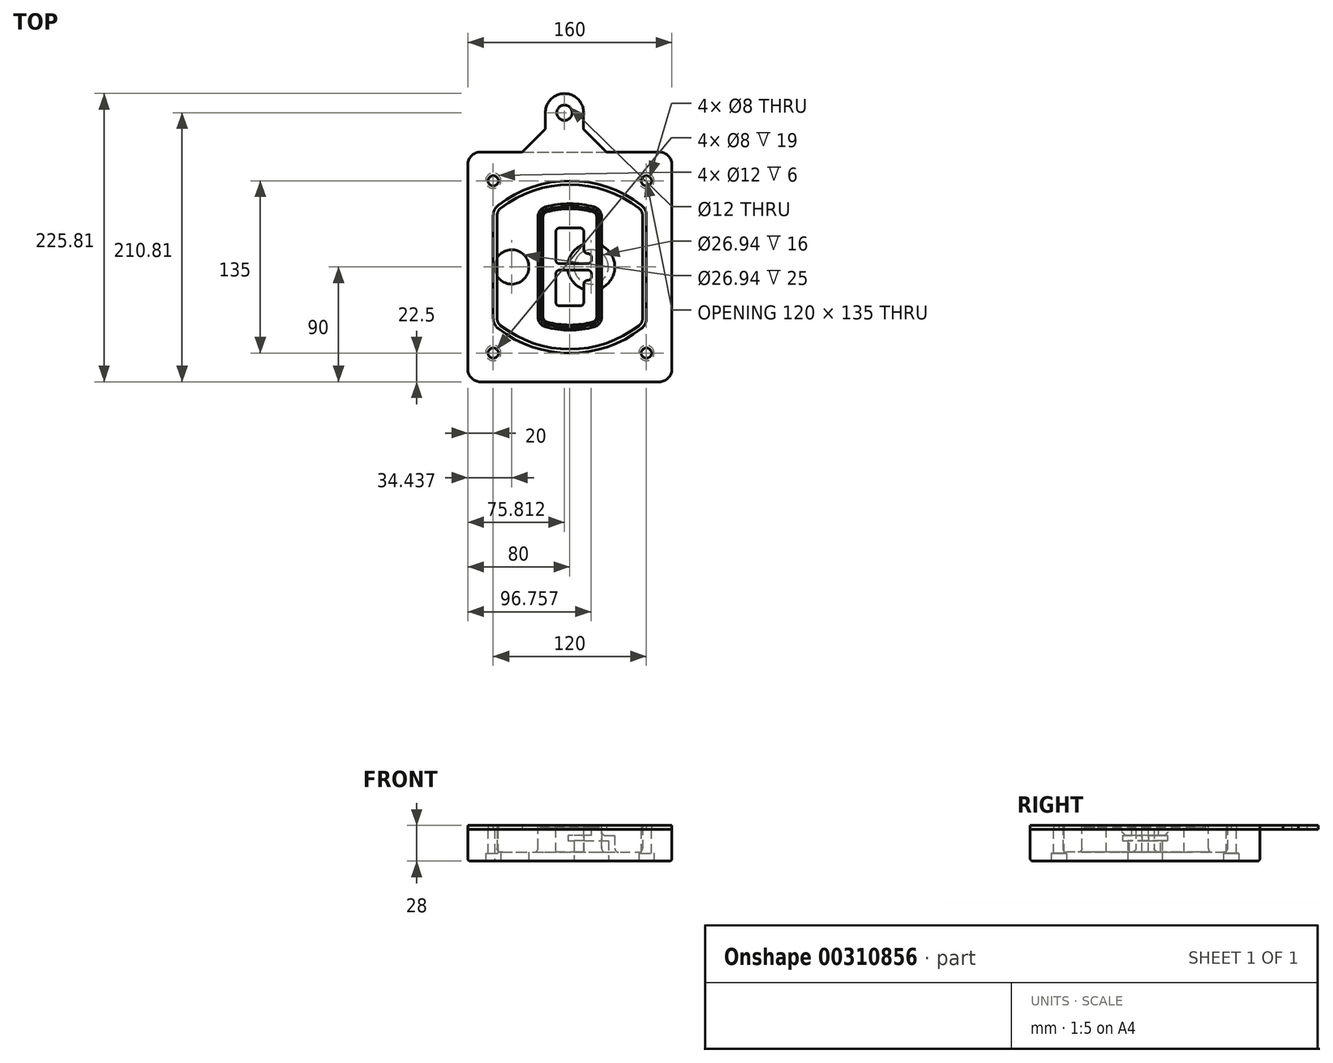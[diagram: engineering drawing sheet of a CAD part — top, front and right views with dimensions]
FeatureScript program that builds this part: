
annotation { "Feature Type Name" : "Feature", "Feature Type Description" : "" }
export const myFeature = defineFeature(function(context is Context, id is Id, definition is map)
    precondition{}
    {
        {
            var Q0;
            Q0=qCreatedBy(makeId("Top.planeOp"),FACE);
            var sketch = newSketch(context, id + "F0", { "sketchPlane" : qUnion([Q0])});
            skPoint(sketch, "E0.rect.middle", {"position": v(0, 0) * mm});
            skLineSegment(sketch, "E1.bottom", {"start": v(-70, -90) * mm, "end": v(70, -90) * mm});
            skLineSegment(sketch, "E1.top", {"start": v(-70, 90) * mm, "end": v(70, 90) * mm});
            skLineSegment(sketch, "E1.left", {"start": v(-80, -80) * mm, "end": v(-80, 80) * mm});
            skLineSegment(sketch, "E1.right", {"start": v(80, -80) * mm, "end": v(80, 80) * mm});
            skLineSegment(sketch, "E2", {"start": v(-80, 90) * mm, "end": v(80, -90) * mm, "construction": true});
            skLineSegment(sketch, "E3", {"start": v(80, 90) * mm, "end": v(-80, -90) * mm, "construction": true});
            skCircle(sketch, "E4", {"center": v(-60, 67.5) * mm, "radius": 4 * mm});
            skCircle(sketch, "E5", {"center": v(60, 67.5) * mm, "radius": 4 * mm});
            skCircle(sketch, "E6", {"center": v(60, -67.5) * mm, "radius": 4 * mm});
            skCircle(sketch, "E7", {"center": v(-60, -67.5) * mm, "radius": 4 * mm});
            skLineSegment(sketch, "E8", {"start": v(-60, 67.5) * mm, "end": v(60, 67.5) * mm, "construction": true});
            skLineSegment(sketch, "E9", {"start": v(60, 67.5) * mm, "end": v(60, -67.5) * mm, "construction": true});
            skLineSegment(sketch, "E10", {"start": v(60, -67.5) * mm, "end": v(-60, -67.5) * mm, "construction": true});
            skLineSegment(sketch, "E11", {"start": v(-60, -67.5) * mm, "end": v(-60, 67.5) * mm, "construction": true});
            skLineSegment(sketch, "E12", {"start": v(-60, 40.3) * mm, "end": v(-60, -40.3) * mm});
            skLineSegment(sketch, "E13", {"start": v(60, 40.3) * mm, "end": v(60, -40.3) * mm});
            skArc(sketch, "E14", {"start": v(56.15, 48.18) * mm, "mid": v(0, 67.5) * mm, "end": v(-56.15, 48.18) * mm});
            skArc(sketch, "E15", {"start": v(-56.15, -48.18) * mm, "mid": v(0, -67.5) * mm, "end": v(56.15, -48.18) * mm});
            skLineSegment(sketch, "E16", {"start": v(-60, 0) * mm, "end": v(60, 0) * mm, "construction": true});
            skPoint(sketch, "E17.visualSharp", {"position": v(-60, -45) * mm});
            skArc(sketch, "E17.filletArc", {"start": v(-60, -40.3) * mm, "mid": v(-58.99, -44.68) * mm, "end": v(-56.15, -48.18) * mm});
            skPoint(sketch, "E18.visualSharp", {"position": v(-60, 45) * mm});
            skArc(sketch, "E18.filletArc", {"start": v(-56.15, 48.18) * mm, "mid": v(-58.99, 44.68) * mm, "end": v(-60, 40.3) * mm});
            skPoint(sketch, "E19.visualSharp", {"position": v(60, 45) * mm});
            skArc(sketch, "E19.filletArc", {"start": v(60, 40.3) * mm, "mid": v(58.99, 44.68) * mm, "end": v(56.15, 48.18) * mm});
            skPoint(sketch, "E20.visualSharp", {"position": v(60, -45) * mm});
            skArc(sketch, "E20.filletArc", {"start": v(56.15, -48.18) * mm, "mid": v(58.99, -44.68) * mm, "end": v(60, -40.3) * mm});
            skPoint(sketch, "E21.visualSharp", {"position": v(-80, 90) * mm});
            skArc(sketch, "E21.filletArc", {"start": v(-70, 90) * mm, "mid": v(-77.07, 87.07) * mm, "end": v(-80, 80) * mm});
            skPoint(sketch, "E22.visualSharp", {"position": v(80, 90) * mm});
            skArc(sketch, "E22.filletArc", {"start": v(80, 80) * mm, "mid": v(77.07, 87.07) * mm, "end": v(70, 90) * mm});
            skPoint(sketch, "E23.visualSharp", {"position": v(80, -90) * mm});
            skArc(sketch, "E23.filletArc", {"start": v(70, -90) * mm, "mid": v(77.07, -87.07) * mm, "end": v(80, -80) * mm});
            skPoint(sketch, "E24.visualSharp", {"position": v(-80, -90) * mm});
            skArc(sketch, "E24.filletArc", {"start": v(-80, -80) * mm, "mid": v(-77.07, -87.07) * mm, "end": v(-70, -90) * mm});
            skArc(sketch, "E25.0", {"start": v(57, 40.3) * mm, "mid": v(56.3, 43.36) * mm, "end": v(54.3, 45.81) * mm});
            skLineSegment(sketch, "E25.1", {"start": v(57, 40.3) * mm, "end": v(57, -40.3) * mm});
            skArc(sketch, "E25.2", {"start": v(54.3, -45.81) * mm, "mid": v(56.3, -43.36) * mm, "end": v(57, -40.3) * mm});
            skArc(sketch, "E25.3", {"start": v(-54.3, -45.81) * mm, "mid": v(0, -64.5) * mm, "end": v(54.3, -45.81) * mm});
            skArc(sketch, "E25.4", {"start": v(-57, -40.3) * mm, "mid": v(-56.3, -43.36) * mm, "end": v(-54.3, -45.81) * mm});
            skArc(sketch, "E25.5", {"start": v(54.3, 45.81) * mm, "mid": v(0, 64.5) * mm, "end": v(-54.3, 45.81) * mm});
            skLineSegment(sketch, "E25.6", {"start": v(-57, 40.3) * mm, "end": v(-57, -40.3) * mm});
            skArc(sketch, "E25.7", {"start": v(-54.3, 45.81) * mm, "mid": v(-56.3, 43.36) * mm, "end": v(-57, 40.3) * mm});
            skArc(sketch, "E26.0", {"start": v(-58.62, 51.33) * mm, "mid": v(-62.58, 46.43) * mm, "end": v(-64, 40.3) * mm});
            skArc(sketch, "E26.1", {"start": v(58.62, 51.33) * mm, "mid": v(0, 71.5) * mm, "end": v(-58.62, 51.33) * mm});
            skArc(sketch, "E26.2", {"start": v(64, 40.3) * mm, "mid": v(62.58, 46.43) * mm, "end": v(58.62, 51.33) * mm});
            skLineSegment(sketch, "E26.3", {"start": v(64, 40.3) * mm, "end": v(64, -40.3) * mm});
            skArc(sketch, "E26.4", {"start": v(58.62, -51.33) * mm, "mid": v(62.58, -46.43) * mm, "end": v(64, -40.3) * mm});
            skLineSegment(sketch, "E26.5", {"start": v(-64, 40.3) * mm, "end": v(-64, -40.3) * mm});
            skArc(sketch, "E26.6", {"start": v(-58.62, -51.33) * mm, "mid": v(0, -71.5) * mm, "end": v(58.62, -51.33) * mm});
            skArc(sketch, "E26.7", {"start": v(-64, -40.3) * mm, "mid": v(-62.58, -46.43) * mm, "end": v(-58.62, -51.33) * mm});
            skSolve(sketch);
        }
        {
            var Q0;
            Q0=makeQuery(id+"F0.imprint","IMPRINT",FACE,{"disambiguationData":[TD([[makeQuery(id+"F0.imprint","IMPRINT",EDGE,{"derivedFrom":sQuery(id+"F0.wireOp",EDGE,"E1.bottom")}),1.0]])]});
            var Q1;
            Q1=makeQuery(id+"F0.imprint","IMPRINT",FACE,{"disambiguationData":[TD([[makeQuery(id+"F0.imprint","IMPRINT",EDGE,{"derivedFrom":sQuery(id+"F0.wireOp",EDGE,"E12")}),1.0]])]});
            var Q2;
            Q2=makeQuery(id+"F0.imprint","IMPRINT",FACE,{"disambiguationData":[TD([[makeQuery(id+"F0.imprint","IMPRINT",EDGE,{"derivedFrom":sQuery(id+"F0.wireOp",EDGE,"E25.0")}),1.0]])]});
            var Q3;
            Q3=makeQuery(id+"F0.imprint","IMPRINT",FACE,{"disambiguationData":[TD([[makeQuery(id+"F0.imprint","IMPRINT",EDGE,{"derivedFrom":sQuery(id+"F0.wireOp",EDGE,"E12")}),-1.0]])]});
            extrude(context, id + "F1", {"entities" : qUnion([Q0, Q1, Q2, Q3]), "oppositeDirection" : true, "depth" : 25 * mm});
        }
        {
            var Q0;
            Q0=makeQuery(id+"F0.imprint","IMPRINT",FACE,{"disambiguationData":[TD([[makeQuery(id+"F0.imprint","IMPRINT",EDGE,{"derivedFrom":sQuery(id+"F0.wireOp",EDGE,"E12")}),1.0]])]});
            extrude(context, id + "F2", {"entities" : qUnion([Q0]), "operationType" : NewBodyOperationType.ADD, "depth" : 3 * mm});
        }
        {
            var Q0;
            Q0=makeQuery(id+"F0.imprint","IMPRINT",FACE,{"disambiguationData":[TD([[makeQuery(id+"F0.imprint","IMPRINT",EDGE,{"derivedFrom":sQuery(id+"F0.wireOp",EDGE,"E25.0")}),1.0]])]});
            extrude(context, id + "F3", {"entities" : qUnion([Q0]), "operationType" : NewBodyOperationType.REMOVE, "oppositeDirection" : true, "depth" : 18 * mm});
        }
        {
            var Q0;
            Q0=makeQuery(id+"F2.opExtrude","CAP_FACE",FACE,{"disambiguationData":[OSD([sQuery(id+"F0.wireOp",EDGE,"E12"),sQuery(id+"F0.wireOp",EDGE,"E13"),sQuery(id+"F0.wireOp",EDGE,"E14"),sQuery(id+"F0.wireOp",EDGE,"E15"),sQuery(id+"F0.wireOp",EDGE,"E17.filletArc"),sQuery(id+"F0.wireOp",EDGE,"E18.filletArc"),sQuery(id+"F0.wireOp",EDGE,"E19.filletArc"),sQuery(id+"F0.wireOp",EDGE,"E20.filletArc"),sQuery(id+"F0.wireOp",EDGE,"E25.0"),sQuery(id+"F0.wireOp",EDGE,"E25.1"),sQuery(id+"F0.wireOp",EDGE,"E25.2"),sQuery(id+"F0.wireOp",EDGE,"E25.3"),sQuery(id+"F0.wireOp",EDGE,"E25.4"),sQuery(id+"F0.wireOp",EDGE,"E25.5"),sQuery(id+"F0.wireOp",EDGE,"E25.6"),sQuery(id+"F0.wireOp",EDGE,"E25.7")])],"isStart":false});
            var sketch = newSketch(context, id + "F4", { "sketchPlane" : qUnion([Q0])});
            skArc(sketch, "E27.0", {"start": v(-19.08, -46.97) * mm, "mid": v(0, -49.5) * mm, "end": v(19.08, -46.97) * mm});
            skArc(sketch, "E28.0", {"start": v(19.08, 46.97) * mm, "mid": v(0, 49.5) * mm, "end": v(-19.08, 46.97) * mm});
            skLineSegment(sketch, "E29", {"start": v(-25, 39.25) * mm, "end": v(-25, -39.25) * mm});
            skLineSegment(sketch, "E30", {"start": v(25, 39.25) * mm, "end": v(25, -39.25) * mm});
            skLineSegment(sketch, "E31", {"start": v(-25, 45.1) * mm, "end": v(25, 45.1) * mm, "construction": true});
            skLineSegment(sketch, "E32", {"start": v(-25, -45.1) * mm, "end": v(25, -45.1) * mm, "construction": true});
            skPoint(sketch, "E33.visualSharp", {"position": v(-25, 45.1) * mm});
            skArc(sketch, "E33.filletArc", {"start": v(-19.08, 46.97) * mm, "mid": v(-23.35, 44.11) * mm, "end": v(-25, 39.25) * mm});
            skPoint(sketch, "E34.visualSharp", {"position": v(25, 45.1) * mm});
            skArc(sketch, "E34.filletArc", {"start": v(25, 39.25) * mm, "mid": v(23.35, 44.11) * mm, "end": v(19.08, 46.97) * mm});
            skPoint(sketch, "E35.visualSharp", {"position": v(25, -45.1) * mm});
            skArc(sketch, "E35.filletArc", {"start": v(19.08, -46.97) * mm, "mid": v(23.35, -44.11) * mm, "end": v(25, -39.25) * mm});
            skPoint(sketch, "E36.visualSharp", {"position": v(-25, -45.1) * mm});
            skArc(sketch, "E36.filletArc", {"start": v(-25, -39.25) * mm, "mid": v(-23.35, -44.11) * mm, "end": v(-19.08, -46.97) * mm});
            skArc(sketch, "E37.0", {"start": v(54.3, 45.81) * mm, "mid": v(0, 64.5) * mm, "end": v(-54.3, 45.81) * mm});
            skArc(sketch, "E37.1", {"start": v(-54.3, 45.81) * mm, "mid": v(-56.3, 43.36) * mm, "end": v(-57, 40.3) * mm});
            skLineSegment(sketch, "E37.2", {"start": v(-57, 40.3) * mm, "end": v(-57, -40.3) * mm});
            skArc(sketch, "E37.3", {"start": v(-57, -40.3) * mm, "mid": v(-56.3, -43.36) * mm, "end": v(-54.3, -45.81) * mm});
            skArc(sketch, "E37.4", {"start": v(-54.3, -45.81) * mm, "mid": v(0, -64.5) * mm, "end": v(54.3, -45.81) * mm});
            skArc(sketch, "E37.5", {"start": v(54.3, -45.81) * mm, "mid": v(56.3, -43.36) * mm, "end": v(57, -40.3) * mm});
            skLineSegment(sketch, "E37.6", {"start": v(57, 40.3) * mm, "end": v(57, -40.3) * mm});
            skArc(sketch, "E37.7", {"start": v(57, 40.3) * mm, "mid": v(56.3, 43.36) * mm, "end": v(54.3, 45.81) * mm});
            skLineSegment(sketch, "E38.0", {"start": v(23, 39.25) * mm, "end": v(23, -39.25) * mm});
            skArc(sketch, "E38.1", {"start": v(18.56, -45.04) * mm, "mid": v(21.76, -42.9) * mm, "end": v(23, -39.25) * mm});
            skArc(sketch, "E38.2", {"start": v(-18.56, -45.04) * mm, "mid": v(0, -47.5) * mm, "end": v(18.56, -45.04) * mm});
            skArc(sketch, "E38.3", {"start": v(-23, -39.25) * mm, "mid": v(-21.76, -42.9) * mm, "end": v(-18.56, -45.04) * mm});
            skLineSegment(sketch, "E38.4", {"start": v(-23, 39.25) * mm, "end": v(-23, -39.25) * mm});
            skArc(sketch, "E38.5", {"start": v(23, 39.25) * mm, "mid": v(21.76, 42.9) * mm, "end": v(18.56, 45.04) * mm});
            skArc(sketch, "E38.6", {"start": v(-18.56, 45.04) * mm, "mid": v(-21.76, 42.9) * mm, "end": v(-23, 39.25) * mm});
            skArc(sketch, "E38.7", {"start": v(18.56, 45.04) * mm, "mid": v(0, 47.5) * mm, "end": v(-18.56, 45.04) * mm});
            skArc(sketch, "E39.0", {"start": v(21, 39.25) * mm, "mid": v(20.18, 41.68) * mm, "end": v(18.04, 43.1) * mm});
            skLineSegment(sketch, "E39.1", {"start": v(21, 39.25) * mm, "end": v(21, -39.25) * mm});
            skArc(sketch, "E39.2", {"start": v(18.04, -43.1) * mm, "mid": v(20.18, -41.68) * mm, "end": v(21, -39.25) * mm});
            skArc(sketch, "E39.3", {"start": v(-18.04, -43.1) * mm, "mid": v(0, -45.5) * mm, "end": v(18.04, -43.1) * mm});
            skArc(sketch, "E39.4", {"start": v(-21, -39.25) * mm, "mid": v(-20.18, -41.68) * mm, "end": v(-18.04, -43.1) * mm});
            skArc(sketch, "E39.5", {"start": v(18.04, 43.1) * mm, "mid": v(0, 45.5) * mm, "end": v(-18.04, 43.1) * mm});
            skLineSegment(sketch, "E39.6", {"start": v(-21, 39.25) * mm, "end": v(-21, -39.25) * mm});
            skArc(sketch, "E39.7", {"start": v(-18.04, 43.1) * mm, "mid": v(-20.18, 41.68) * mm, "end": v(-21, 39.25) * mm});
            skLineSegment(sketch, "E40", {"start": v(-25, 0) * mm, "end": v(25, 0) * mm, "construction": true});
            skLineSegment(sketch, "E41", {"start": v(-11, 5.5) * mm, "end": v(-11, 27.5) * mm});
            skLineSegment(sketch, "E42", {"start": v(-8, 30.5) * mm, "end": v(8, 30.5) * mm});
            skLineSegment(sketch, "E43", {"start": v(11, 27.5) * mm, "end": v(11, 13.5) * mm});
            skLineSegment(sketch, "E44", {"start": v(14, 10.5) * mm, "end": v(14, 10.5) * mm});
            skLineSegment(sketch, "E45", {"start": v(17, 7.5) * mm, "end": v(17, 5.5) * mm});
            skLineSegment(sketch, "E46", {"start": v(14, 2.5) * mm, "end": v(-8, 2.5) * mm});
            skPoint(sketch, "E47.visualSharp", {"position": v(-11, 30.5) * mm});
            skArc(sketch, "E47.filletArc", {"start": v(-8, 30.5) * mm, "mid": v(-10.12, 29.62) * mm, "end": v(-11, 27.5) * mm});
            skPoint(sketch, "E48.visualSharp", {"position": v(11, 30.5) * mm});
            skArc(sketch, "E48.filletArc", {"start": v(11, 27.5) * mm, "mid": v(10.12, 29.62) * mm, "end": v(8, 30.5) * mm});
            skPoint(sketch, "E49.visualSharp", {"position": v(11, 10.5) * mm});
            skArc(sketch, "E49.filletArc", {"start": v(11, 13.5) * mm, "mid": v(11.88, 11.38) * mm, "end": v(14, 10.5) * mm});
            skPoint(sketch, "E50.visualSharp", {"position": v(17, 10.5) * mm});
            skArc(sketch, "E50.filletArc", {"start": v(17, 7.5) * mm, "mid": v(16.12, 9.62) * mm, "end": v(14, 10.5) * mm});
            skPoint(sketch, "E51.visualSharp", {"position": v(17, 2.5) * mm});
            skArc(sketch, "E51.filletArc", {"start": v(14, 2.5) * mm, "mid": v(16.12, 3.38) * mm, "end": v(17, 5.5) * mm});
            skPoint(sketch, "E52.visualSharp", {"position": v(-11, 2.5) * mm});
            skArc(sketch, "E52.filletArc", {"start": v(-11, 5.5) * mm, "mid": v(-10.12, 3.38) * mm, "end": v(-8, 2.5) * mm});
            skLineSegment(sketch, "E53.0.MirrorCS", {"start": v(14, -2.5) * mm, "end": v(-8, -2.5) * mm});
            skArc(sketch, "E54.0.MirrorCS", {"start": v(-11, -5.5) * mm, "mid": v(-10.12, -3.38) * mm, "end": v(-8, -2.5) * mm});
            skLineSegment(sketch, "E55.0.MirrorCS", {"start": v(-11, -5.5) * mm, "end": v(-11, -27.5) * mm});
            skArc(sketch, "E56.0.MirrorCS", {"start": v(-8, -30.5) * mm, "mid": v(-10.12, -29.62) * mm, "end": v(-11, -27.5) * mm});
            skLineSegment(sketch, "E57.0.MirrorCS", {"start": v(-8, -30.5) * mm, "end": v(8, -30.5) * mm});
            skArc(sketch, "E58.0.MirrorCS", {"start": v(11, -27.5) * mm, "mid": v(10.12, -29.62) * mm, "end": v(8, -30.5) * mm});
            skLineSegment(sketch, "E59.0.MirrorCS", {"start": v(11, -27.5) * mm, "end": v(11, -13.5) * mm});
            skArc(sketch, "E60.0.MirrorCS", {"start": v(11, -13.5) * mm, "mid": v(11.88, -11.38) * mm, "end": v(14, -10.5) * mm});
            skArc(sketch, "E61.0.MirrorCS", {"start": v(17, -7.5) * mm, "mid": v(16.12, -9.62) * mm, "end": v(14, -10.5) * mm});
            skLineSegment(sketch, "E62.0.MirrorCS", {"start": v(17, -7.5) * mm, "end": v(17, -5.5) * mm});
            skArc(sketch, "E63.0.MirrorCS", {"start": v(14, -2.5) * mm, "mid": v(16.12, -3.38) * mm, "end": v(17, -5.5) * mm});
            skSolve(sketch);
        }
        {
            var Q0;
            Q0=makeQuery(id+"F4.imprint","IMPRINT",FACE,{"disambiguationData":[TD([[makeQuery(id+"F4.imprint","IMPRINT",EDGE,{"derivedFrom":sQuery(id+"F4.wireOp",EDGE,"E27.0")}),1.0]])]});
            var Q1;
            Q1=makeQuery(id+"F4.imprint","IMPRINT",FACE,{"disambiguationData":[TD([[makeQuery(id+"F4.imprint","IMPRINT",EDGE,{"derivedFrom":sQuery(id+"F4.wireOp",EDGE,"E38.0")}),-1.0]])]});
            var Q2;
            Q2=makeQuery(id+"F4.imprint","IMPRINT",FACE,{"disambiguationData":[TD([[makeQuery(id+"F4.imprint","IMPRINT",EDGE,{"derivedFrom":sQuery(id+"F4.wireOp",EDGE,"E39.0")}),1.0]])]});
            extrude(context, id + "F5", {"entities" : qUnion([Q0, Q1, Q2]), "operationType" : NewBodyOperationType.ADD, "endBound" : BoundingType.UP_TO_NEXT, "oppositeDirection" : true, "depth" : 25 * mm});
        }
        {
            var Q0;
            Q0=makeQuery(id+"F4.imprint","IMPRINT",FACE,{"disambiguationData":[TD([[makeQuery(id+"F4.imprint","IMPRINT",EDGE,{"derivedFrom":sQuery(id+"F4.wireOp",EDGE,"E38.0")}),-1.0]])]});
            extrude(context, id + "F6", {"entities" : qUnion([Q0]), "operationType" : NewBodyOperationType.REMOVE, "oppositeDirection" : true, "depth" : 2 * mm});
        }
        {
            var Q0;
            Q0=makeQuery(id+"F1.opExtrude","CAP_FACE",FACE,{"disambiguationData":[OSD([sQuery(id+"F0.wireOp",EDGE,"E1.bottom"),sQuery(id+"F0.wireOp",EDGE,"E1.top"),sQuery(id+"F0.wireOp",EDGE,"E1.left"),sQuery(id+"F0.wireOp",EDGE,"E1.right"),sQuery(id+"F0.wireOp",EDGE,"E4"),sQuery(id+"F0.wireOp",EDGE,"E5"),sQuery(id+"F0.wireOp",EDGE,"E6"),sQuery(id+"F0.wireOp",EDGE,"E7"),sQuery(id+"F0.wireOp",EDGE,"E21.filletArc"),sQuery(id+"F0.wireOp",EDGE,"E22.filletArc"),sQuery(id+"F0.wireOp",EDGE,"E23.filletArc"),sQuery(id+"F0.wireOp",EDGE,"E24.filletArc")])],"isStart":false});
            var sketch = newSketch(context, id + "F7", { "sketchPlane" : qUnion([Q0])});
            skCircle(sketch, "E64", {"center": v(16.76, 0) * mm, "radius": 13.47 * mm});
            skCircle(sketch, "E65", {"center": v(-45.56, 0) * mm, "radius": 13.47 * mm});
            skLineSegment(sketch, "E66", {"start": v(80, 0) * mm, "end": v(-80, 0) * mm});
            skCircle(sketch, "E67", {"center": v(16.76, 0) * mm, "radius": 18.47 * mm});
            skCircle(sketch, "E68", {"center": v(60, -67.5) * mm, "radius": 6 * mm});
            skCircle(sketch, "E69", {"center": v(-60, -67.5) * mm, "radius": 6 * mm});
            skCircle(sketch, "E70", {"center": v(-60, 67.5) * mm, "radius": 6 * mm});
            skCircle(sketch, "E71", {"center": v(60, 67.5) * mm, "radius": 6 * mm});
            skSolve(sketch);
        }
        {
            var Q0;
            {var subQ1=sQuery(id+"F7.wireOp",EDGE,"E66");var subQ4=sQuery(id+"F7.wireOp",EDGE,"E64");var subQ6=makeQuery(id+"F7.imprint","INTERSECT",VERTEX,{"disambiguationData":[OD(0.0)],"derivedFrom":[subQ4,subQ1]});Q0=makeQuery(id+"F7.imprint","IMPRINT",FACE,{"disambiguationData":[TD([[makeQuery(id+"F7.imprint","IMPRINT",EDGE,{"disambiguationData":[TD([[subQ6,-1.0]])],"derivedFrom":subQ4}),-1.0]])]});}
            var Q1;
            {var subQ0=sQuery(id+"F7.wireOp",EDGE,"E66");var subQ1=sQuery(id+"F7.wireOp",EDGE,"E64");var subQ3=makeQuery(id+"F7.imprint","INTERSECT",VERTEX,{"disambiguationData":[OD(0.0)],"derivedFrom":[subQ1,subQ0]});Q1=makeQuery(id+"F7.imprint","IMPRINT",FACE,{"disambiguationData":[TD([[makeQuery(id+"F7.imprint","IMPRINT",EDGE,{"disambiguationData":[TD([[subQ3,-1.0]])],"derivedFrom":subQ1}),1.0]])]});}
            var Q2;
            {var subQ0=sQuery(id+"F7.wireOp",EDGE,"E66");var subQ1=sQuery(id+"F7.wireOp",EDGE,"E64");var subQ3=makeQuery(id+"F7.imprint","INTERSECT",VERTEX,{"disambiguationData":[OD(0.0)],"derivedFrom":[subQ1,subQ0]});Q2=makeQuery(id+"F7.imprint","IMPRINT",FACE,{"disambiguationData":[TD([[makeQuery(id+"F7.imprint","IMPRINT",EDGE,{"disambiguationData":[TD([[subQ3,1.0]])],"derivedFrom":subQ1}),1.0]])]});}
            var Q3;
            {var subQ1=sQuery(id+"F7.wireOp",EDGE,"E66");var subQ4=sQuery(id+"F7.wireOp",EDGE,"E64");var subQ6=makeQuery(id+"F7.imprint","INTERSECT",VERTEX,{"disambiguationData":[OD(0.0)],"derivedFrom":[subQ4,subQ1]});Q3=makeQuery(id+"F7.imprint","IMPRINT",FACE,{"disambiguationData":[TD([[makeQuery(id+"F7.imprint","IMPRINT",EDGE,{"disambiguationData":[TD([[subQ6,1.0]])],"derivedFrom":subQ4}),-1.0]])]});}
            extrude(context, id + "F8", {"entities" : qUnion([Q0, Q1, Q2, Q3]), "operationType" : NewBodyOperationType.ADD, "oppositeDirection" : true, "depth" : 20 * mm});
        }
        {
            var Q0;
            {var subQ0=sQuery(id+"F7.wireOp",EDGE,"E66");var subQ1=sQuery(id+"F7.wireOp",EDGE,"E64");var subQ3=makeQuery(id+"F7.imprint","INTERSECT",VERTEX,{"disambiguationData":[OD(0.0)],"derivedFrom":[subQ1,subQ0]});Q0=makeQuery(id+"F7.imprint","IMPRINT",FACE,{"disambiguationData":[TD([[makeQuery(id+"F7.imprint","IMPRINT",EDGE,{"disambiguationData":[TD([[subQ3,-1.0]])],"derivedFrom":subQ1}),1.0]])]});}
            var Q1;
            {var subQ0=sQuery(id+"F7.wireOp",EDGE,"E66");var subQ1=sQuery(id+"F7.wireOp",EDGE,"E64");var subQ3=makeQuery(id+"F7.imprint","INTERSECT",VERTEX,{"disambiguationData":[OD(0.0)],"derivedFrom":[subQ1,subQ0]});Q1=makeQuery(id+"F7.imprint","IMPRINT",FACE,{"disambiguationData":[TD([[makeQuery(id+"F7.imprint","IMPRINT",EDGE,{"disambiguationData":[TD([[subQ3,1.0]])],"derivedFrom":subQ1}),1.0]])]});}
            extrude(context, id + "F9", {"entities" : qUnion([Q0, Q1]), "operationType" : NewBodyOperationType.REMOVE, "oppositeDirection" : true, "depth" : 16 * mm});
        }
        {
            var Q0;
            {var subQ0=sQuery(id+"F7.wireOp",EDGE,"E66");var subQ1=sQuery(id+"F7.wireOp",EDGE,"E65");var subQ3=makeQuery(id+"F7.imprint","INTERSECT",VERTEX,{"disambiguationData":[OD(0.0)],"derivedFrom":[subQ1,subQ0]});Q0=makeQuery(id+"F7.imprint","IMPRINT",FACE,{"disambiguationData":[TD([[makeQuery(id+"F7.imprint","IMPRINT",EDGE,{"disambiguationData":[TD([[subQ3,-1.0]])],"derivedFrom":subQ1}),1.0]])]});}
            var Q1;
            {var subQ0=sQuery(id+"F7.wireOp",EDGE,"E66");var subQ1=sQuery(id+"F7.wireOp",EDGE,"E65");var subQ3=makeQuery(id+"F7.imprint","INTERSECT",VERTEX,{"disambiguationData":[OD(0.0)],"derivedFrom":[subQ1,subQ0]});Q1=makeQuery(id+"F7.imprint","IMPRINT",FACE,{"disambiguationData":[TD([[makeQuery(id+"F7.imprint","IMPRINT",EDGE,{"disambiguationData":[TD([[subQ3,1.0]])],"derivedFrom":subQ1}),1.0]])]});}
            extrude(context, id + "F10", {"entities" : qUnion([Q0, Q1]), "operationType" : NewBodyOperationType.REMOVE, "oppositeDirection" : true, "depth" : 25 * mm});
        }
        {
            var Q0;
            Q0=makeQuery(id+"F7.imprint","IMPRINT",FACE,{"disambiguationData":[TD([[makeQuery(id+"F7.imprint","IMPRINT",EDGE,{"derivedFrom":sQuery(id+"F7.wireOp",EDGE,"E68")}),1.0]])]});
            var Q1;
            Q1=makeQuery(id+"F7.imprint","IMPRINT",FACE,{"disambiguationData":[TD([[makeQuery(id+"F7.imprint","IMPRINT",EDGE,{"derivedFrom":makeQuery(id+"F1.opExtrude","CAP_EDGE",EDGE,{"disambiguationData":[OSD([sQuery(id+"F0.wireOp",EDGE,"E5")])],"isStart":false})}),-1.0]])]});
            var Q2;
            Q2=makeQuery(id+"F7.imprint","IMPRINT",FACE,{"disambiguationData":[TD([[makeQuery(id+"F7.imprint","IMPRINT",EDGE,{"derivedFrom":sQuery(id+"F7.wireOp",EDGE,"E69")}),1.0]])]});
            var Q3;
            Q3=makeQuery(id+"F7.imprint","IMPRINT",FACE,{"disambiguationData":[TD([[makeQuery(id+"F7.imprint","IMPRINT",EDGE,{"derivedFrom":makeQuery(id+"F1.opExtrude","CAP_EDGE",EDGE,{"disambiguationData":[OSD([sQuery(id+"F0.wireOp",EDGE,"E4")])],"isStart":false})}),-1.0]])]});
            var Q4;
            Q4=makeQuery(id+"F7.imprint","IMPRINT",FACE,{"disambiguationData":[TD([[makeQuery(id+"F7.imprint","IMPRINT",EDGE,{"derivedFrom":sQuery(id+"F7.wireOp",EDGE,"E70")}),1.0]])]});
            var Q5;
            Q5=makeQuery(id+"F7.imprint","IMPRINT",FACE,{"disambiguationData":[TD([[makeQuery(id+"F7.imprint","IMPRINT",EDGE,{"derivedFrom":makeQuery(id+"F1.opExtrude","CAP_EDGE",EDGE,{"disambiguationData":[OSD([sQuery(id+"F0.wireOp",EDGE,"E7")])],"isStart":false})}),-1.0]])]});
            var Q6;
            Q6=makeQuery(id+"F7.imprint","IMPRINT",FACE,{"disambiguationData":[TD([[makeQuery(id+"F7.imprint","IMPRINT",EDGE,{"derivedFrom":sQuery(id+"F7.wireOp",EDGE,"E71")}),1.0]])]});
            var Q7;
            Q7=makeQuery(id+"F7.imprint","IMPRINT",FACE,{"disambiguationData":[TD([[makeQuery(id+"F7.imprint","IMPRINT",EDGE,{"derivedFrom":makeQuery(id+"F1.opExtrude","CAP_EDGE",EDGE,{"disambiguationData":[OSD([sQuery(id+"F0.wireOp",EDGE,"E6")])],"isStart":false})}),-1.0]])]});
            extrude(context, id + "F11", {"entities" : qUnion([Q0, Q1, Q2, Q3, Q4, Q5, Q6, Q7]), "operationType" : NewBodyOperationType.REMOVE, "oppositeDirection" : true, "depth" : 6 * mm});
        }
        {
            var Q0;
            Q0=makeQuery(id+"F9.boolean.opBoolean","COPY",FACE,{"derivedFrom":makeQuery(id+"F9.opExtrude","CAP_FACE",FACE,{"disambiguationData":[OSD([sQuery(id+"F7.wireOp",EDGE,"E64")])],"isStart":false})});
            var sketch = newSketch(context, id + "F12", { "sketchPlane" : qUnion([Q0])});
            skArc(sketch, "E72.0", {"start": v(11, 17.55) * mm, "mid": v(2.57, 11.82) * mm, "end": v(-1.54, 2.5) * mm});
            skArc(sketch, "E72.1", {"start": v(-1.54, -2.5) * mm, "mid": v(2.57, -11.82) * mm, "end": v(11, -17.55) * mm});
            skLineSegment(sketch, "E73", {"start": v(-1.54, -2.5) * mm, "end": v(14, -2.5) * mm});
            skLineSegment(sketch, "E74.0", {"start": v(14, 2.5) * mm, "end": v(-1.54, 2.5) * mm});
            skArc(sketch, "E74.1", {"start": v(14, 2.5) * mm, "mid": v(16.12, 3.38) * mm, "end": v(17, 5.5) * mm});
            skLineSegment(sketch, "E74.2", {"start": v(17, 7.5) * mm, "end": v(17, 5.5) * mm});
            skArc(sketch, "E74.3", {"start": v(17, 7.5) * mm, "mid": v(16.12, 9.62) * mm, "end": v(14, 10.5) * mm});
            skArc(sketch, "E74.4", {"start": v(11, 13.5) * mm, "mid": v(11.88, 11.38) * mm, "end": v(14, 10.5) * mm});
            skLineSegment(sketch, "E74.5", {"start": v(11, 17.55) * mm, "end": v(11, 13.5) * mm});
            skLineSegment(sketch, "E74.7", {"start": v(14, -2.5) * mm, "end": v(-1.54, -2.5) * mm});
            skArc(sketch, "E74.8", {"start": v(14, -2.5) * mm, "mid": v(16.12, -3.38) * mm, "end": v(17, -5.5) * mm});
            skLineSegment(sketch, "E74.9", {"start": v(17, -7.5) * mm, "end": v(17, -5.5) * mm});
            skArc(sketch, "E74.10", {"start": v(17, -7.5) * mm, "mid": v(16.12, -9.62) * mm, "end": v(14, -10.5) * mm});
            skArc(sketch, "E74.11", {"start": v(11, -13.5) * mm, "mid": v(11.88, -11.38) * mm, "end": v(14, -10.5) * mm});
            skLineSegment(sketch, "E74.12", {"start": v(11, -17.55) * mm, "end": v(11, -13.5) * mm});
            skPoint(sketch, "E75.orphan", {"position": v(11, -27.5) * mm});
            skPoint(sketch, "E76.orphan", {"position": v(-8, -2.5) * mm});
            skPoint(sketch, "E77.orphan", {"position": v(-8, 2.5) * mm});
            skPoint(sketch, "E78.orphan", {"position": v(11, 27.5) * mm});
            skSolve(sketch);
        }
        {
            var Q0;
            {var subQ7=sQuery(id+"F12.wireOp",EDGE,"E72.0");var subQ14=sQuery(id+"F12.wireOp",EDGE,"E72.1");var subQ16=sQuery(id+"F12.wireOp",EDGE,"E74.1");var subQ18=sQuery(id+"F12.wireOp",EDGE,"E74.8");Q0=qUnion([makeQuery(id+"F12.imprint","IMPRINT",FACE,{"disambiguationData":[TD([[makeQuery(id+"F12.imprint","IMPRINT",EDGE,{"derivedFrom":subQ7}),1.0]])]}),makeQuery(id+"F12.imprint","IMPRINT",FACE,{"disambiguationData":[TD([[makeQuery(id+"F12.imprint","IMPRINT",EDGE,{"derivedFrom":subQ14}),1.0]])]}),makeQuery(id+"F12.imprint","IMPRINT",FACE,{"disambiguationData":[TD([[makeQuery(id+"F12.imprint","IMPRINT",EDGE,{"derivedFrom":subQ16}),1.0]])]}),makeQuery(id+"F12.imprint","IMPRINT",FACE,{"disambiguationData":[TD([[makeQuery(id+"F12.imprint","IMPRINT",EDGE,{"derivedFrom":subQ18}),-1.0]])]})]);}
            var Q1;
            Q1=makeQuery(id+"F5.boolean.opBoolean","SPLIT",FACE,{"disambiguationData":[TD([makeQuery(id+"F5.opExtrude","SWEPT_FACE",FACE,{"disambiguationData":[OSD([sQuery(id+"F4.wireOp",EDGE,"E41")])]})])],"derivedFrom":makeQuery(id+"F3.boolean.opBoolean","COPY",FACE,{"derivedFrom":makeQuery(id+"F3.opExtrude","CAP_FACE",FACE,{"disambiguationData":[OSD([sQuery(id+"F0.wireOp",EDGE,"E25.0"),sQuery(id+"F0.wireOp",EDGE,"E25.1"),sQuery(id+"F0.wireOp",EDGE,"E25.2"),sQuery(id+"F0.wireOp",EDGE,"E25.3"),sQuery(id+"F0.wireOp",EDGE,"E25.4"),sQuery(id+"F0.wireOp",EDGE,"E25.5"),sQuery(id+"F0.wireOp",EDGE,"E25.6"),sQuery(id+"F0.wireOp",EDGE,"E25.7")])],"isStart":false})})});
            extrude(context, id + "F13", {"entities" : qUnion([Q0]), "operationType" : NewBodyOperationType.REMOVE, "endBound" : BoundingType.UP_TO_SURFACE, "endBoundEntityFace" : qUnion([Q1]), "depth" : 25 * mm});
        }
        {
            var Q0;
            Q0=makeQuery(id+"F3.boolean.opBoolean","COPY",EDGE,{"derivedFrom":makeQuery(id+"F3.opExtrude","CAP_EDGE",EDGE,{"disambiguationData":[OSD([sQuery(id+"F0.wireOp",EDGE,"E25.6")])],"isStart":false})});
            var Q1;
            Q1=makeQuery(id+"F8.boolean.opBoolean","INTERSECT",EDGE,{"derivedFrom":[makeQuery(id+"F5.opExtrude","SWEPT_FACE",FACE,{"disambiguationData":[OSD([sQuery(id+"F4.wireOp",EDGE,"E30")])]}),makeQuery(id+"F8.opExtrude","CAP_FACE",FACE,{"disambiguationData":[OSD([sQuery(id+"F7.wireOp",EDGE,"E67")])],"isStart":false})]});
            var Q2;
            Q2=makeQuery(id+"F8.boolean.opBoolean","INTERSECT",EDGE,{"disambiguationData":[OD(1.0)],"derivedFrom":[makeQuery(id+"F5.opExtrude","SWEPT_FACE",FACE,{"disambiguationData":[OSD([sQuery(id+"F4.wireOp",EDGE,"E30")])]}),makeQuery(id+"F8.opExtrude","SWEPT_FACE",FACE,{"disambiguationData":[OSD([sQuery(id+"F7.wireOp",EDGE,"E67")])]})]});
            var Q3;
            {var subQ0=sQuery(id+"F4.wireOp",EDGE,"E30");Q3=makeQuery(id+"F8.boolean.opBoolean","SPLIT",EDGE,{"disambiguationData":[TD([makeQuery(id+"F5.opExtrude","SWEPT_FACE",FACE,{"disambiguationData":[OSD([sQuery(id+"F4.wireOp",EDGE,"E35.filletArc")])]})])],"derivedFrom":makeQuery(id+"F5.opExtrude","CAP_EDGE",EDGE,{"disambiguationData":[OSD([subQ0])],"isStart":false})});}
            var Q4;
            {var subQ0=sQuery(id+"F0.wireOp",EDGE,"E25.7");var subQ1=sQuery(id+"F0.wireOp",EDGE,"E25.1");var subQ2=sQuery(id+"F0.wireOp",EDGE,"E25.6");var subQ3=sQuery(id+"F0.wireOp",EDGE,"E25.5");var subQ4=sQuery(id+"F0.wireOp",EDGE,"E25.4");var subQ5=sQuery(id+"F0.wireOp",EDGE,"E25.0");var subQ6=sQuery(id+"F0.wireOp",EDGE,"E25.2");var subQ7=sQuery(id+"F0.wireOp",EDGE,"E25.3");Q4=makeQuery(id+"F8.boolean.opBoolean","INTERSECT",EDGE,{"derivedFrom":[makeQuery(id+"F5.boolean.opBoolean","SPLIT",FACE,{"disambiguationData":[TD([makeQuery(id+"F2.opExtrude","SWEPT_FACE",FACE,{"disambiguationData":[OSD([subQ5])]})])],"derivedFrom":makeQuery(id+"F3.boolean.opBoolean","COPY",FACE,{"derivedFrom":makeQuery(id+"F3.opExtrude","CAP_FACE",FACE,{"disambiguationData":[OSD([subQ5,subQ1,subQ6,subQ7,subQ4,subQ3,subQ2,subQ0])],"isStart":false})})}),makeQuery(id+"F8.opExtrude","SWEPT_FACE",FACE,{"disambiguationData":[OSD([sQuery(id+"F7.wireOp",EDGE,"E67")])]})]});}
            var Q5;
            Q5=makeQuery(id+"F8.boolean.opBoolean","INTERSECT",EDGE,{"disambiguationData":[OD(0.0)],"derivedFrom":[makeQuery(id+"F5.opExtrude","SWEPT_FACE",FACE,{"disambiguationData":[OSD([sQuery(id+"F4.wireOp",EDGE,"E30")])]}),makeQuery(id+"F8.opExtrude","SWEPT_FACE",FACE,{"disambiguationData":[OSD([sQuery(id+"F7.wireOp",EDGE,"E67")])]})]});
            fillet(context, id + "F14", {"entities" : qUnion([Q0, Q1, Q2, Q3, Q4, Q5]), "radius" : 3 * mm, "tangentPropagation" : true, "allowEdgeOverflow" : false});
        }
        {
            var Q0;
            Q0=makeQuery(id+"F1.opExtrude","CAP_EDGE",EDGE,{"disambiguationData":[OSD([sQuery(id+"F0.wireOp",EDGE,"E1.bottom")])],"isStart":false});
            fillet(context, id + "F15", {"entities" : qUnion([Q0]), "radius" : 2 * mm, "tangentPropagation" : true, "allowEdgeOverflow" : false});
        }
        {
            var Q0;
            {var subQ0=sQuery(id+"F0.wireOp",EDGE,"E21.filletArc");var subQ1=sQuery(id+"F0.wireOp",EDGE,"E7");var subQ2=sQuery(id+"F0.wireOp",EDGE,"E6");var subQ3=sQuery(id+"F0.wireOp",EDGE,"E5");var subQ4=sQuery(id+"F0.wireOp",EDGE,"E4");var subQ5=sQuery(id+"F0.wireOp",EDGE,"E22.filletArc");var subQ6=sQuery(id+"F0.wireOp",EDGE,"E1.bottom");var subQ7=sQuery(id+"F0.wireOp",EDGE,"E1.right");var subQ8=sQuery(id+"F0.wireOp",EDGE,"E1.top");var subQ9=sQuery(id+"F0.wireOp",EDGE,"E1.left");var subQ10=sQuery(id+"F0.wireOp",EDGE,"E23.filletArc");var subQ11=sQuery(id+"F0.wireOp",EDGE,"E24.filletArc");Q0=makeQuery(id+"F2.boolean.opBoolean","SPLIT",FACE,{"disambiguationData":[TD([makeQuery(id+"F1.opExtrude","SWEPT_FACE",FACE,{"disambiguationData":[OSD([subQ6])]})])],"derivedFrom":makeQuery(id+"F1.opExtrude","CAP_FACE",FACE,{"disambiguationData":[OSD([subQ6,subQ8,subQ9,subQ7,subQ4,subQ3,subQ2,subQ1,subQ0,subQ5,subQ10,subQ11])],"isStart":true})});}
            var sketch = newSketch(context, id + "F16", { "sketchPlane" : qUnion([Q0])});
            skArc(sketch, "E79", {"start": v(10.8, 120) * mm, "mid": v(-4.19, 135.8) * mm, "end": v(-19.17, 120) * mm});
            skPoint(sketch, "E80.end.orphan", {"position": v(-12.9, 108.78) * mm});
            skPoint(sketch, "E81.start.orphan", {"position": v(17.1, 108.78) * mm});
            skPoint(sketch, "E82.start.orphan", {"position": v(18.56, 108) * mm});
            skPoint(sketch, "E83.end.orphan", {"position": v(-11.44, 108) * mm});
            skLineSegment(sketch, "E84", {"start": v(-19.17, 120) * mm, "end": v(-19.17, 108) * mm});
            skLineSegment(sketch, "E85", {"start": v(-19.17, 108) * mm, "end": v(-37.17, 90) * mm});
            skLineSegment(sketch, "E86", {"start": v(10.8, 120) * mm, "end": v(10.8, 108) * mm});
            skLineSegment(sketch, "E87", {"start": v(10.8, 108) * mm, "end": v(28.8, 90) * mm});
            skLineSegment(sketch, "E88", {"start": v(-80, 0) * mm, "end": v(80, 0) * mm, "construction": true});
            skCircle(sketch, "E89", {"center": v(-4.19, 120.8) * mm, "radius": 6 * mm});
            skPoint(sketch, "E90.end.orphan", {"position": v(0, 110.52) * mm});
            skPoint(sketch, "E90.start.orphan", {"position": v(0, 0) * mm});
            skLineSegment(sketch, "E91", {"start": v(-4.19, 120.8) * mm, "end": v(-4.19, 90) * mm, "construction": true});
            skArc(sketch, "E92.MirrorCS", {"start": v(10.8, -120) * mm, "mid": v(-4.19, -135.8) * mm, "end": v(-19.17, -120) * mm});
            skLineSegment(sketch, "E93.MirrorCS", {"start": v(10.8, -120) * mm, "end": v(10.8, -108) * mm});
            skLineSegment(sketch, "E94.MirrorCS", {"start": v(-19.17, -120) * mm, "end": v(-19.17, -108) * mm});
            skLineSegment(sketch, "E95.MirrorCS", {"start": v(-19.17, -108) * mm, "end": v(-37.17, -90) * mm});
            skLineSegment(sketch, "E96.MirrorCS", {"start": v(10.8, -108) * mm, "end": v(28.8, -90) * mm});
            skLineSegment(sketch, "E97.MirrorCS", {"start": v(-4.19, -120.8) * mm, "end": v(-4.19, -90) * mm, "construction": true});
            skCircle(sketch, "E98", {"center": v(-4.19, -120.8) * mm, "radius": 6 * mm});
            skSolve(sketch);
        }
        {
            var Q0;
            Q0=makeQuery(id+"F16.imprint","IMPRINT",FACE,{"disambiguationData":[TD([[makeQuery(id+"F16.imprint","IMPRINT",EDGE,{"derivedFrom":sQuery(id+"F16.wireOp",EDGE,"Hgsh0Pt0-c17b-b6FX-Ninl-LV6eHDRzl9ee")}),-1.0]])]});
            var Q1;
            Q1=makeQuery(id+"F16.imprint","IMPRINT",FACE,{"disambiguationData":[TD([[makeQuery(id+"F16.imprint","IMPRINT",EDGE,{"derivedFrom":makeQuery(id+"F1.opExtrude","CAP_EDGE",EDGE,{"disambiguationData":[OSD([sQuery(id+"F0.wireOp",EDGE,"E1.left")])],"isStart":true})}),-1.0]])]});
            var Q2;
            {var subQ1=sQuery(id+"F16.wireOp",EDGE,"757e7bbc-6e4c-4edf-8524-ce2efe46098d0.MirrorCS");Q2=makeQuery(id+"F16.imprint","IMPRINT",FACE,{"disambiguationData":[TD([[makeQuery(id+"F16.imprint","IMPRINT",EDGE,{"derivedFrom":subQ1}),-1.0]])]});}
            var Q3;
            Q3=makeQuery(id+"F16.imprint","IMPRINT",FACE,{"disambiguationData":[TD([[makeQuery(id+"F16.imprint","IMPRINT",EDGE,{"derivedFrom":sQuery(id+"F16.wireOp",EDGE,"E79")}),1.0]])]});
            var Q4;
            Q4=makeQuery(id+"F16.imprint","IMPRINT",FACE,{"disambiguationData":[TD([[makeQuery(id+"F16.imprint","IMPRINT",EDGE,{"derivedFrom":sQuery(id+"F16.wireOp",EDGE,"E92.MirrorCS")}),-1.0]])]});
            var Q5;
            Q5=makeQuery(id+"F2.opExtrude","CAP_FACE",FACE,{"disambiguationData":[OSD([sQuery(id+"F0.wireOp",EDGE,"E12"),sQuery(id+"F0.wireOp",EDGE,"E13"),sQuery(id+"F0.wireOp",EDGE,"E14"),sQuery(id+"F0.wireOp",EDGE,"E15"),sQuery(id+"F0.wireOp",EDGE,"E17.filletArc"),sQuery(id+"F0.wireOp",EDGE,"E18.filletArc"),sQuery(id+"F0.wireOp",EDGE,"E19.filletArc"),sQuery(id+"F0.wireOp",EDGE,"E20.filletArc"),sQuery(id+"F0.wireOp",EDGE,"E25.0"),sQuery(id+"F0.wireOp",EDGE,"E25.1"),sQuery(id+"F0.wireOp",EDGE,"E25.2"),sQuery(id+"F0.wireOp",EDGE,"E25.3"),sQuery(id+"F0.wireOp",EDGE,"E25.4"),sQuery(id+"F0.wireOp",EDGE,"E25.5"),sQuery(id+"F0.wireOp",EDGE,"E25.6"),sQuery(id+"F0.wireOp",EDGE,"E25.7")])],"isStart":false});
            extrude(context, id + "F17", {"entities" : qUnion([Q0, Q1, Q2, Q3, Q4]), "endBound" : BoundingType.UP_TO_SURFACE, "endBoundEntityFace" : qUnion([Q5]), "depth" : 25 * mm});
        }
    });
